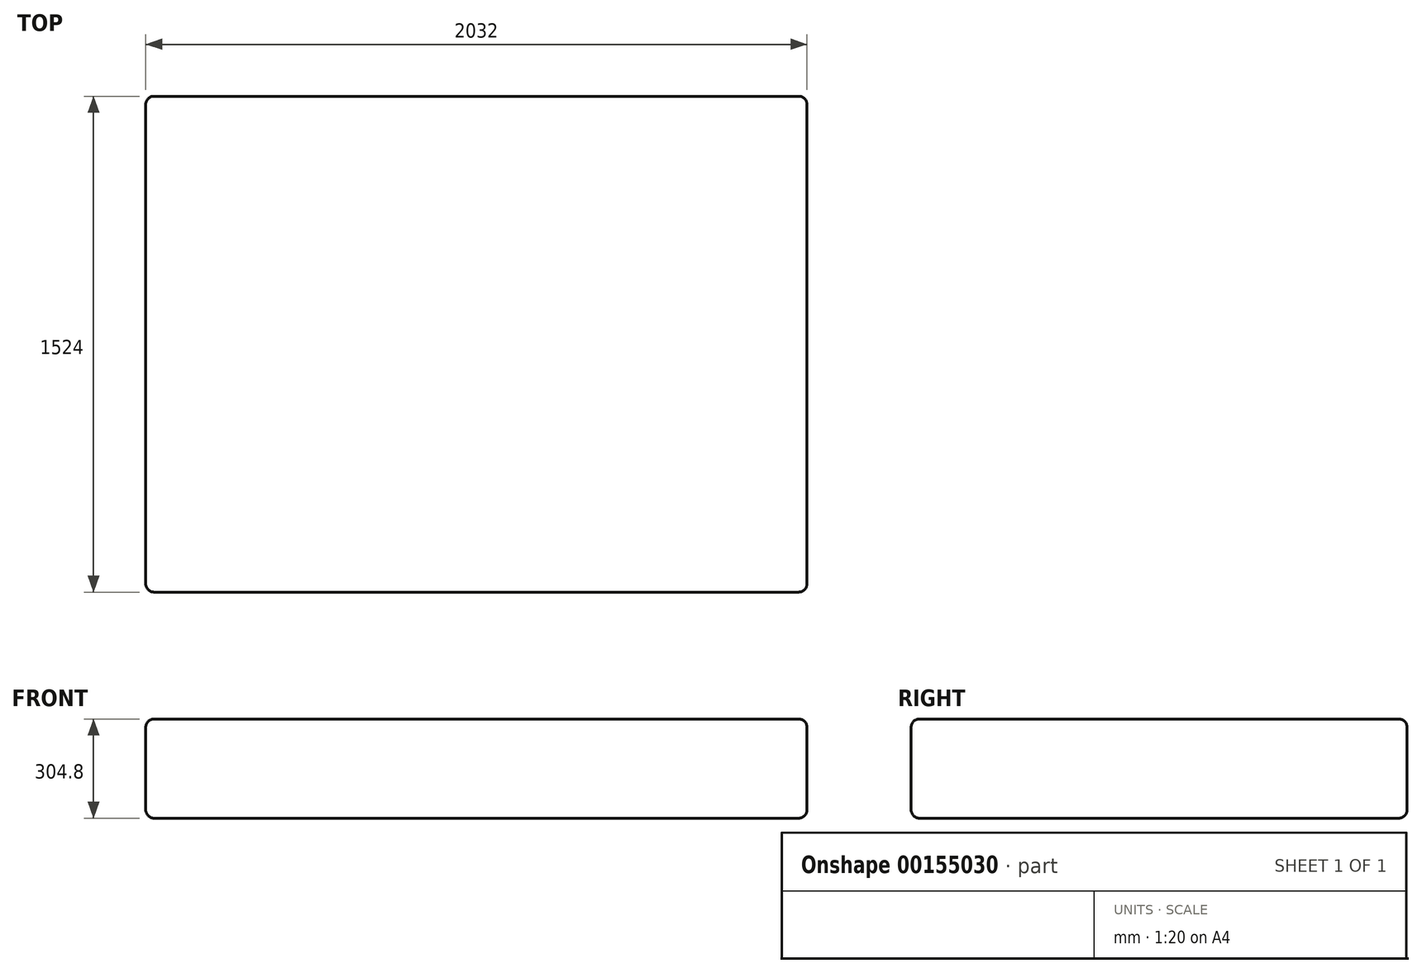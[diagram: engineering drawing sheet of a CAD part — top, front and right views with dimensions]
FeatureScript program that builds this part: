
annotation { "Feature Type Name" : "Feature", "Feature Type Description" : "" }
export const myFeature = defineFeature(function(context is Context, id is Id, definition is map)
    precondition{}
    {
        {
            var Q0;
            Q0=qCreatedBy(makeId("Top.planeOp"),FACE);
            var sketch = newSketch(context, id + "F0", { "sketchPlane" : qUnion([Q0])});
            skLineSegment(sketch, "E0.bottom", {"start": v(25.4, 0) * mm, "end": v(2006.6, 0) * mm});
            skLineSegment(sketch, "E0.top", {"start": v(25.4, 1524) * mm, "end": v(2006.6, 1524) * mm});
            skLineSegment(sketch, "E0.left", {"start": v(0, 25.4) * mm, "end": v(0, 1498.6) * mm});
            skLineSegment(sketch, "E0.right", {"start": v(2032, 25.4) * mm, "end": v(2032, 1498.6) * mm});
            skPoint(sketch, "E1.visualSharp", {"position": v(0, 1524) * mm});
            skArc(sketch, "E1.filletArc", {"start": v(25.4, 1524) * mm, "mid": v(7.44, 1516.56) * mm, "end": v(0, 1498.6) * mm});
            skPoint(sketch, "E2.visualSharp", {"position": v(2032, 1524) * mm});
            skArc(sketch, "E2.filletArc", {"start": v(2032, 1498.6) * mm, "mid": v(2024.56, 1516.56) * mm, "end": v(2006.6, 1524) * mm});
            skPoint(sketch, "E3.visualSharp", {"position": v(2032, 0) * mm});
            skArc(sketch, "E3.filletArc", {"start": v(2006.6, 0) * mm, "mid": v(2024.56, 7.44) * mm, "end": v(2032, 25.4) * mm});
            skPoint(sketch, "E4.visualSharp", {"position": v(0, 0) * mm});
            skArc(sketch, "E4.filletArc", {"start": v(0, 25.4) * mm, "mid": v(7.44, 7.44) * mm, "end": v(25.4, 0) * mm});
            skSolve(sketch);
        }
        {
            var Q0;
            Q0=makeQuery(id+"F0.imprint","IMPRINT",FACE,{"disambiguationData":[TD([[makeQuery(id+"F0.imprint","IMPRINT",EDGE,{"derivedFrom":sQuery(id+"F0.wireOp",EDGE,"E0.bottom")}),1.0]])]});
            extrude(context, id + "F1", {"entities" : qUnion([Q0]), "depth" : 304.8 * mm});
        }
        {
            var Q0;
            Q0=makeQuery(id+"F1.opExtrude","CAP_EDGE",EDGE,{"disambiguationData":[OSD([sQuery(id+"F0.wireOp",EDGE,"E0.bottom")])],"isStart":false});
            var Q1;
            Q1=makeQuery(id+"F1.opExtrude","CAP_EDGE",EDGE,{"disambiguationData":[OSD([sQuery(id+"F0.wireOp",EDGE,"E0.bottom")])],"isStart":true});
            fillet(context, id + "F2", {"entities" : qUnion([Q0, Q1]), "radius" : 25.4 * mm, "tangentPropagation" : true, "allowEdgeOverflow" : false});
        }
    });
